# Revit family: Zumtobel EPURIA W
name_source: partatom
category: Lighting Fixtures
revit_build: Autodesk Revit 2016 (Build: 20150220_1215(x64)
units: mm (PartAtom-declared; Revit-internal decimal feet)

## family parameters
Cut with Voids When Loaded = No
Host = Face
Light Source = Yes
OmniClass Number = 23.80.70.11
OmniClass Title = Luminaries for Internal Lighting
Part Type = Normal
Room Calculation Point = No
Round Connector Dimension = Use Diameter
Shared = No

## types (1)
- EPURIA W DI 6500-940 WH LDE
    Apparent Load = 55 VA
    Assembly Code = D5020200
    Body = ZG_Metal_White
    Color Filter = 16777215
    Default Elevation = 2000 mm
    Description = LED wall luminaire
    Dimming Lamp Color Temperature Shift = <None>
    Emit Shape Visible in Rendering = Yes
    Emit from Rectangle Length = 120 mm
    Emit from Rectangle Width = 549 mm
    Height = 38 mm
    Lamp = LED
    Length = 629 mm
    Manufacturer = Zumtobel Lighting
    Model = 42187610
    Photometric Web File = 42187610_(STD_LEO).IES
    Reflector = ZG_Metal_White_Self_Illumination
    Tilt Angle = -90.00°
    URL = http://www.zumtobel.com
    Voltage = 230 V
    Width = 200 mm  [stored 0.656168 ft]

note: [stored X ft] marks values corroborated as IEEE doubles in the binary element streams (Revit-internal decimal feet)

## geometry (parser evidence)
native form markers: Sweep x2
no freeform markers — native parametric forms only
